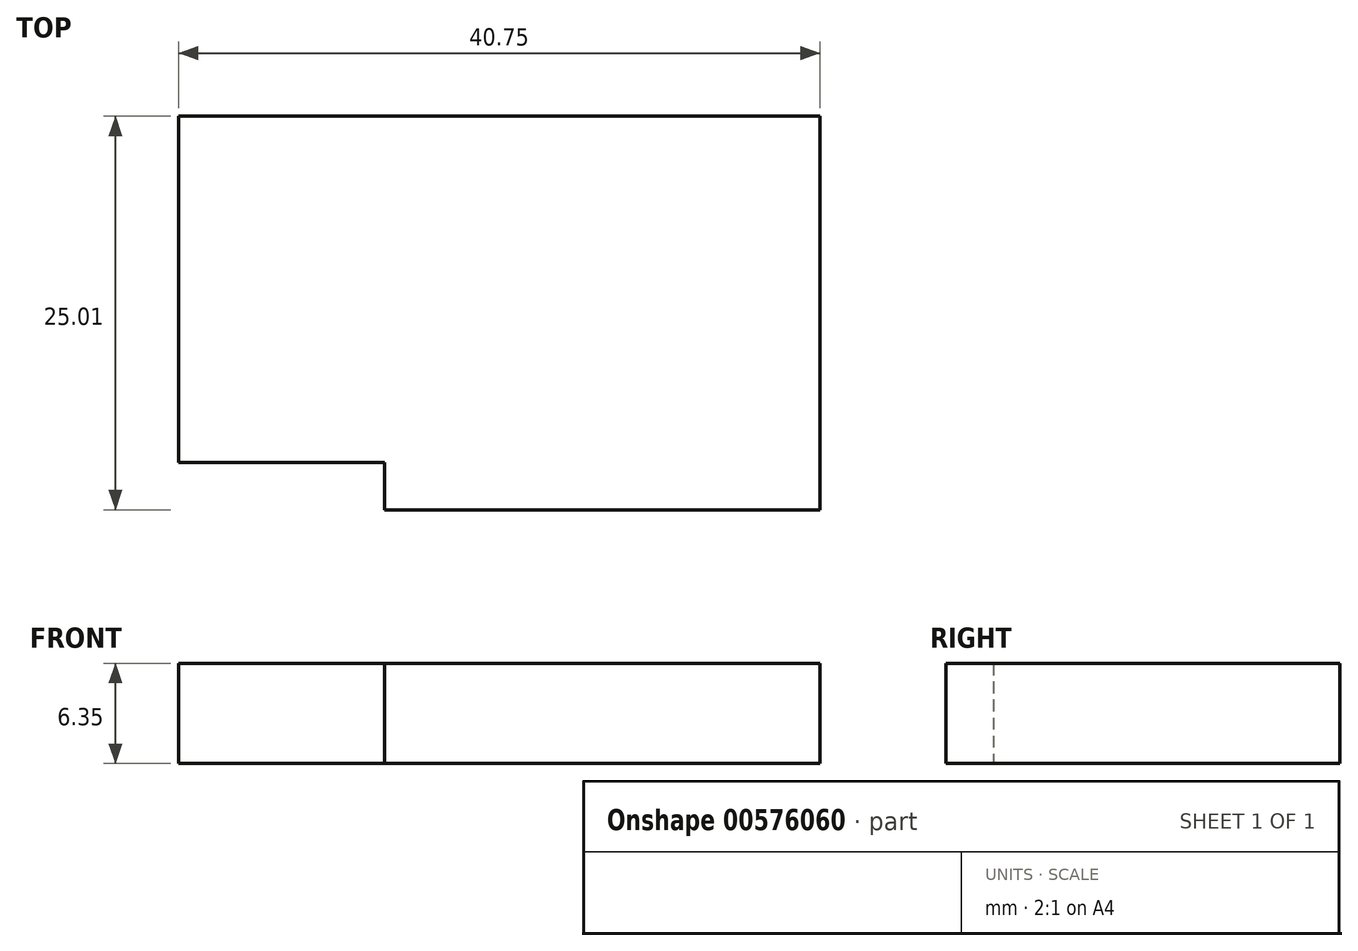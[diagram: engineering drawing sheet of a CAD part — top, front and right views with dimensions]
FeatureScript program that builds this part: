
annotation { "Feature Type Name" : "Feature", "Feature Type Description" : "" }
export const myFeature = defineFeature(function(context is Context, id is Id, definition is map)
    precondition{}
    {
        {
            var Q0;
            Q0=qCreatedBy(makeId("Top.planeOp"),FACE);
            var sketch = newSketch(context, id + "F0", { "sketchPlane" : qUnion([Q0])});
            skLineSegment(sketch, "E0", {"start": v(0, 0) * mm, "end": v(40.75, 0) * mm});
            skLineSegment(sketch, "E1", {"start": v(40.75, 0) * mm, "end": v(40.75, -25) * mm});
            skLineSegment(sketch, "E2", {"start": v(40.75, -25) * mm, "end": v(13.1, -25.01) * mm});
            skLineSegment(sketch, "E3", {"start": v(0, 0) * mm, "end": v(0, -22.01) * mm});
            skLineSegment(sketch, "E4", {"start": v(0, -22.01) * mm, "end": v(13.1, -22) * mm});
            skLineSegment(sketch, "E5", {"start": v(13.1, -22) * mm, "end": v(13.1, -25.01) * mm});
            skSolve(sketch);
        }
        {
            var Q0;
            Q0 = qSketchRegion(id + "F0", true);
            extrude(context, id + "F1", {"entities" : qUnion([Q0]), "depth" : 6.35 * mm, "offsetDistance" : 25 * mm});
        }
    });
